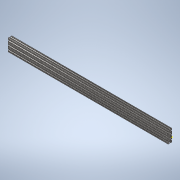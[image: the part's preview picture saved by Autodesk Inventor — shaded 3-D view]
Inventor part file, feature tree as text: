
AUTODESK INVENTOR PART (.ipt)
format: ipt  version: 2020 (Build 240168000, 168)  size: 401,408 bytes
history: native  units: in
note: dims shown in document units (in); Inventor stores cm internally (conversion verified against a paired STEP export)
features: sketch x2, extrude x1
ambient origin geometry x8: Origin, YZ Plane, XZ Plane, XY Plane, X Axis, Y Axis, Z Axis, Center Point
bodies: Solid1 (feature_tree)
feature tree (3):
  extrude  "Extrusion1"  [1 undecoded]
  sketch  "Sketch2"
  sketch  "Sketch1"  dims[d0=39.0in d1=0.0in]
note: 1 required parameter value undecoded (feature->parameter linkage not recoverable at this tier; creation-order binding heuristic only, values carry confidence <= 0.55)
